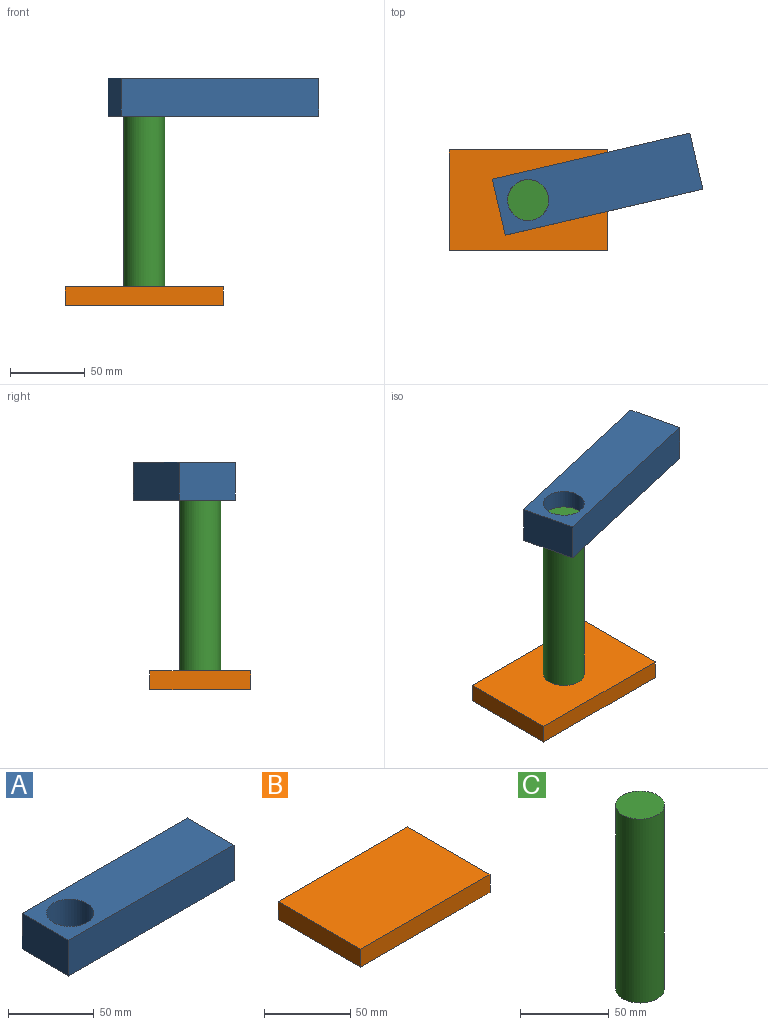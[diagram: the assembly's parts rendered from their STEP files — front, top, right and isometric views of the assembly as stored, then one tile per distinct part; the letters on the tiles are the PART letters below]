
ASSEMBLY  parts=3 mates=2
PART A: 7 faces, bbox 135.9x38.5x25.4 mm
  f0: plane 38.53x25.4mm, normal (-1,0,0), area 978.7mm2, adj f1,f4,f5,f6
  f1: plane 135.87x25.4mm, normal (0,-1,0), area 3451.1mm2, adj f0,f2,f5,f6
  f2: plane 38.53x25.4mm, normal (1,0,0), area 978.7mm2, adj f1,f4,f5,f6
  f3: cylinder r=13.78mm len=27.56mm, axis (0,0,-1), area 2199.1mm2, adj f5,f6
  f4: plane 135.87x25.4mm, normal (0,1,0), area 3451.1mm2, adj f0,f2,f5,f6
  f5: plane 135.87x38.53mm, normal (0,0,1), area 4638.6mm2, adj f0,f1,f2,f3,f4
  f6: plane 135.87x38.53mm, normal (0,0,-1), area 4638.6mm2, adj f0,f1,f2,f3,f4
PART B: 6 faces, bbox 105.9x67.5x12.7 mm
  f0: plane 105.95x12.7mm, normal (0,1,0), area 1345.5mm2, adj f1,f3,f4,f5
  f1: plane 67.53x12.7mm, normal (-1,0,0), area 857.7mm2, adj f0,f2,f4,f5
  f2: plane 105.95x12.7mm, normal (0,-1,0), area 1345.5mm2, adj f1,f3,f4,f5
  f3: plane 67.53x12.7mm, normal (1,0,0), area 857.7mm2, adj f0,f2,f4,f5
  f4: plane 105.95x67.53mm, normal (0,0,1), area 7154.8mm2, adj f0,f1,f2,f3
  f5: plane 105.95x67.53mm, normal (0,0,-1), area 7154.8mm2, adj f0,f1,f2,f3
PART C: 3 faces, bbox 27.6x27.6x127 mm
  f0: cylinder r=13.78mm len=127mm, axis (0,0,-1), area 10995.6mm2, adj f1,f2
  f1: plane 27.56x27.56mm, normal (0,0,1), area 596.5mm2, adj f0
  f2: plane 27.56x27.56mm, normal (0,0,-1), area 596.5mm2, adj f0
PLACE A rot(axis=(0.99,0.11,0),180deg) t=(-81.45,25.71,232.52)mm
PLACE B rot(axis=(-0.24,-0.02,-0.97),0deg) t=(-81.45,25.71,-46.88)mm fixed
PLACE C rot(axis=(-0.24,-0.02,-0.97),0deg) t=(-81.45,25.71,-34.18)mm
MATE revolute A.f3 <-> C.f0  axis (0,0,1) through (-81.45,25.71,92.82)mm
MATE fastened C.f0 <-> B.f4  axis (0,0,-1) through (-81.45,25.71,-34.18)mm
